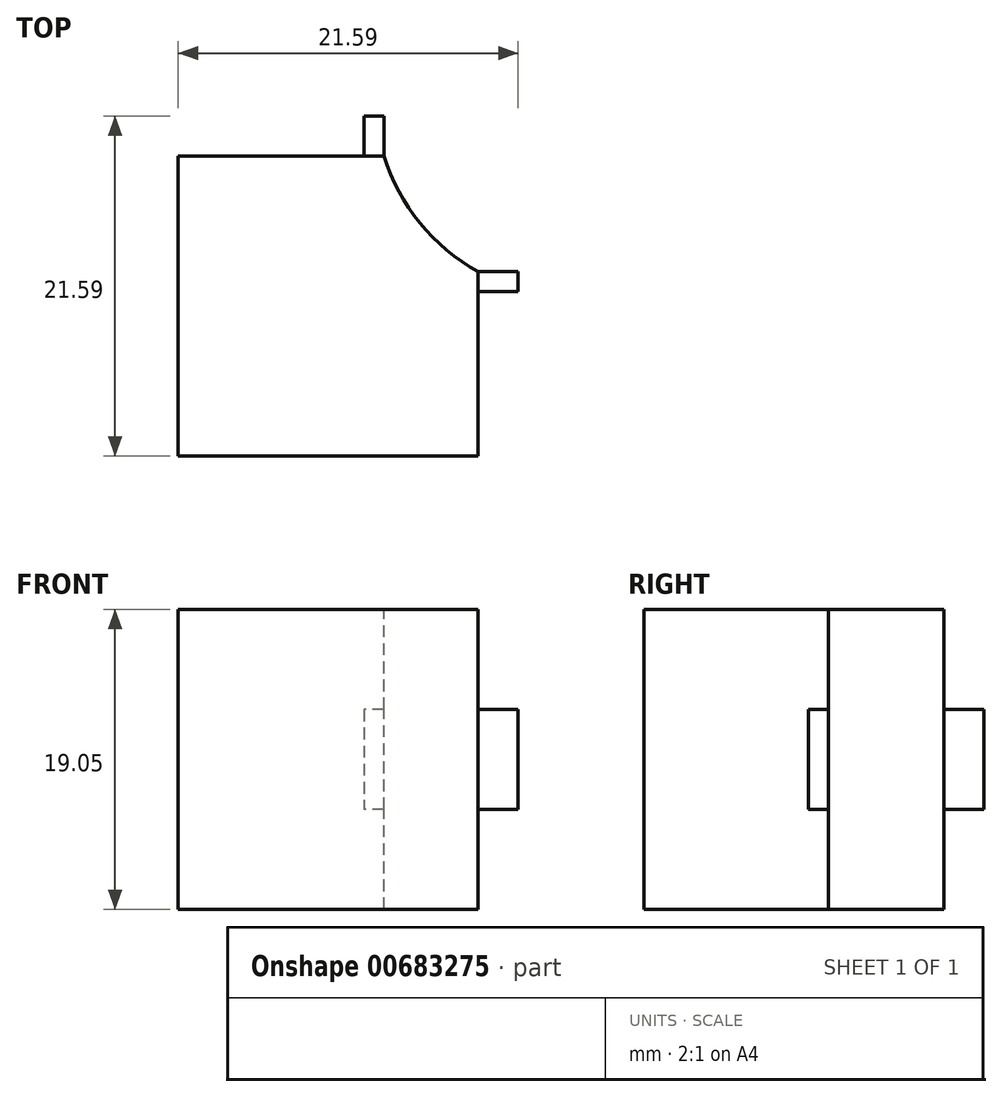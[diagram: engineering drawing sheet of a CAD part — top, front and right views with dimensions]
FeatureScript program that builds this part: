
annotation { "Feature Type Name" : "Feature", "Feature Type Description" : "" }
export const myFeature = defineFeature(function(context is Context, id is Id, definition is map)
    precondition{}
    {
        {
            var Q0;
            Q0=qCreatedBy(makeId("Top.planeOp"),FACE);
            var sketch = newSketch(context, id + "F0", { "sketchPlane" : qUnion([Q0])});
            skLineSegment(sketch, "E0.bottom", {"start": v(-53.28, 62.27) * mm, "end": v(-34.23, 62.27) * mm});
            skLineSegment(sketch, "E0.top", {"start": v(-53.28, 43.22) * mm, "end": v(-34.23, 43.22) * mm});
            skLineSegment(sketch, "E0.left", {"start": v(-53.28, 62.27) * mm, "end": v(-53.28, 43.22) * mm});
            skLineSegment(sketch, "E0.right", {"start": v(-34.23, 62.27) * mm, "end": v(-34.23, 43.22) * mm});
            skSolve(sketch);
        }
        {
            var Q0;
            Q0 = qSketchRegion(id + "F0", true);
            extrude(context, id + "F1", {"entities" : qUnion([Q0]), "depth" : 19.05 * mm, "offsetDistance" : 25.4 * mm});
        }
        {
            var Q0;
            Q0=makeQuery(id+"F1.opExtrude","CAP_FACE",FACE,{"disambiguationData":[OSD([sQuery(id+"F0.wireOp",EDGE,"E0.bottom"),sQuery(id+"F0.wireOp",EDGE,"E0.top"),sQuery(id+"F0.wireOp",EDGE,"E0.left"),sQuery(id+"F0.wireOp",EDGE,"E0.right")])],"isStart":false});
            var sketch = newSketch(context, id + "F2", { "sketchPlane" : qUnion([Q0])});
            skArc(sketch, "E1", {"start": v(-40.2, 62.27) * mm, "mid": v(-37.93, 58.01) * mm, "end": v(-34.23, 54.93) * mm});
            skSolve(sketch);
        }
        {
            var Q0;
            Q0 = qSketchRegion(id + "F2", true);
            var Q1;
            {var subQ0=sQuery(id+"F2.wireOp",EDGE,"E1");Q1=makeQuery(id+"F2.imprint","IMPRINT",FACE,{"disambiguationData":[TD([[makeQuery(id+"F2.imprint","IMPRINT",EDGE,{"derivedFrom":subQ0}),1.0]])]});}
            extrude(context, id + "F3", {"entities" : qUnion([Q0, Q1]), "operationType" : NewBodyOperationType.REMOVE, "oppositeDirection" : true, "depth" : 25.4 * mm, "offsetDistance" : 25.4 * mm});
        }
        {
            var Q0;
            Q0=makeQuery(id+"F1.opExtrude","SWEPT_FACE",FACE,{"disambiguationData":[OSD([sQuery(id+"F0.wireOp",EDGE,"E0.right")])]});
            var sketch = newSketch(context, id + "F4", { "sketchPlane" : qUnion([Q0])});
            skLineSegment(sketch, "E2.bottom", {"start": v(54.93, 12.7) * mm, "end": v(53.66, 12.7) * mm});
            skLineSegment(sketch, "E2.top", {"start": v(54.93, 6.35) * mm, "end": v(53.66, 6.35) * mm});
            skLineSegment(sketch, "E2.left", {"start": v(54.93, 12.7) * mm, "end": v(54.93, 6.35) * mm});
            skLineSegment(sketch, "E2.right", {"start": v(53.66, 12.7) * mm, "end": v(53.66, 6.35) * mm});
            skSolve(sketch);
        }
        {
            var Q0;
            Q0=makeQuery(id+"F4.imprint","IMPRINT",FACE,{"disambiguationData":[TD([[makeQuery(id+"F4.imprint","IMPRINT",EDGE,{"derivedFrom":sQuery(id+"F4.wireOp",EDGE,"E2.bottom")}),1.0]])]});
            extrude(context, id + "F5", {"entities" : qUnion([Q0]), "operationType" : NewBodyOperationType.ADD, "depth" : 2.54 * mm, "offsetDistance" : 25.4 * mm});
        }
        {
            var Q0;
            Q0=makeQuery(id+"F1.opExtrude","SWEPT_FACE",FACE,{"disambiguationData":[OSD([sQuery(id+"F0.wireOp",EDGE,"E0.bottom")])]});
            var sketch = newSketch(context, id + "F6", { "sketchPlane" : qUnion([Q0])});
            skLineSegment(sketch, "E3.bottom", {"start": v(40.2, 12.7) * mm, "end": v(41.47, 12.7) * mm});
            skLineSegment(sketch, "E3.top", {"start": v(40.2, 6.35) * mm, "end": v(41.47, 6.35) * mm});
            skLineSegment(sketch, "E3.left", {"start": v(40.2, 12.7) * mm, "end": v(40.2, 6.35) * mm});
            skLineSegment(sketch, "E3.right", {"start": v(41.47, 12.7) * mm, "end": v(41.47, 6.35) * mm});
            skSolve(sketch);
        }
        {
            var Q0;
            Q0 = qSketchRegion(id + "F6", true);
            extrude(context, id + "F7", {"entities" : qUnion([Q0]), "operationType" : NewBodyOperationType.ADD, "depth" : 2.54 * mm, "offsetDistance" : 25.4 * mm});
        }
    });
